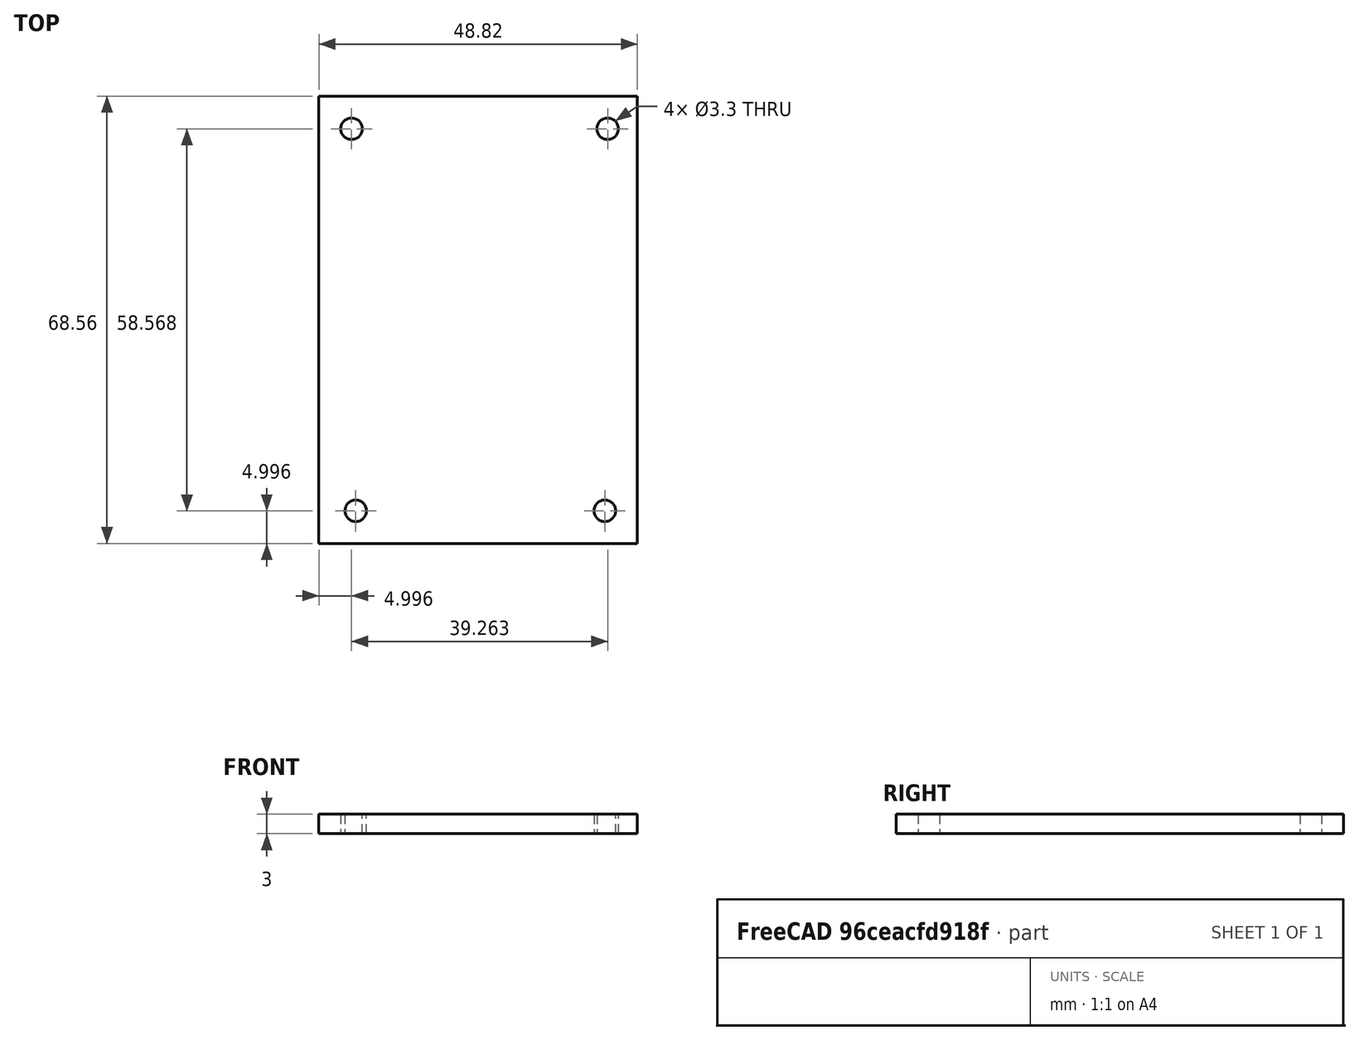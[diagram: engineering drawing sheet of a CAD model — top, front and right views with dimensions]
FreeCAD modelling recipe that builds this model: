
FCSTD DOCUMENT  (FreeCAD 0.21R33694 (Git))
Label: OJT1_T018_P01_placa_4forats
License: All rights reserved
LicenseURL: http://en.wikipedia.org/wiki/All_rights_reserved
objects: Sketcher::SketchObject×1, PartDesign::Pad×1, PartDesign::Body×1
note: 4 computed .brp shape members not serialized (recipe doc carries the construction recipe); baked Part::Feature solids carry a one-line shape summary decoded from their .brp

FEATURE [Sketcher::SketchObject] Sketch
  FullyConstrained = false
  MapMode = 5
  Support = -> [XY_Plane]
  sketch-geometry (8):
    g0: LineSegment StartX=-24.4143 StartY=35.6941 StartZ=0 EndX=24.4143 EndY=35.6941 EndZ=0
    g1: LineSegment StartX=24.4143 StartY=35.6941 StartZ=0 EndX=24.4143 EndY=-32.8742 EndZ=0
    g2: LineSegment StartX=24.4143 StartY=-32.8742 StartZ=0 EndX=-24.4143 EndY=-32.8742 EndZ=0
    g3: LineSegment StartX=-24.4143 StartY=-32.8742 StartZ=0 EndX=-24.4143 EndY=35.6941 EndZ=0
    g4: Circle CenterX=-19.4143 CenterY=30.6941 CenterZ=0 NormalX=0 NormalY=0 NormalZ=1 AngleXU=0 Radius=1.65202
    g5: Circle CenterX=19.8482 CenterY=30.6941 CenterZ=0 NormalX=0 NormalY=0 NormalZ=1 AngleXU=0 Radius=1.65202
    g6: Circle CenterX=19.4143 CenterY=-27.8742 CenterZ=0 NormalX=0 NormalY=0 NormalZ=1 AngleXU=0 Radius=1.65202
    g7: Circle CenterX=-18.7635 CenterY=-27.8742 CenterZ=0 NormalX=0 NormalY=0 NormalZ=1 AngleXU=0 Radius=1.65202
  constraints (16):
    c: Coincident(g0,g1)
    c: Coincident(g1,g2)
    c: Coincident(g2,g3)
    c: Coincident(g3,g0)
    c: Horizontal(g2)
    c: Vertical(g1)
    c: Vertical(g3)
    c: Symmetric(g0,g0,g-2)
    c: Equal(g4,g5)
    c: Equal(g5,g6)
    c: Equal(g6,g7)
    c: DistanceY(g2,g7) = 5
    c: DistanceY(g1,g6) = 5
    c: DistanceY(g4,g0) = 5
    c: DistanceY(g5,g0) = 5
    c: DistanceX(g6,g1) = 5
FEATURE [PartDesign::Pad] Pad
  Direction = (0,0,1)
  Length = 3
  Length2 = 10
  Profile = -> Sketch
  ReferenceAxis = -> Sketch [N_Axis]
  Type = 0
FEATURE [PartDesign::Body] Body
  Group = -> [Sketch,Pad]
  Origin = -> Origin
  Tip = -> Pad
